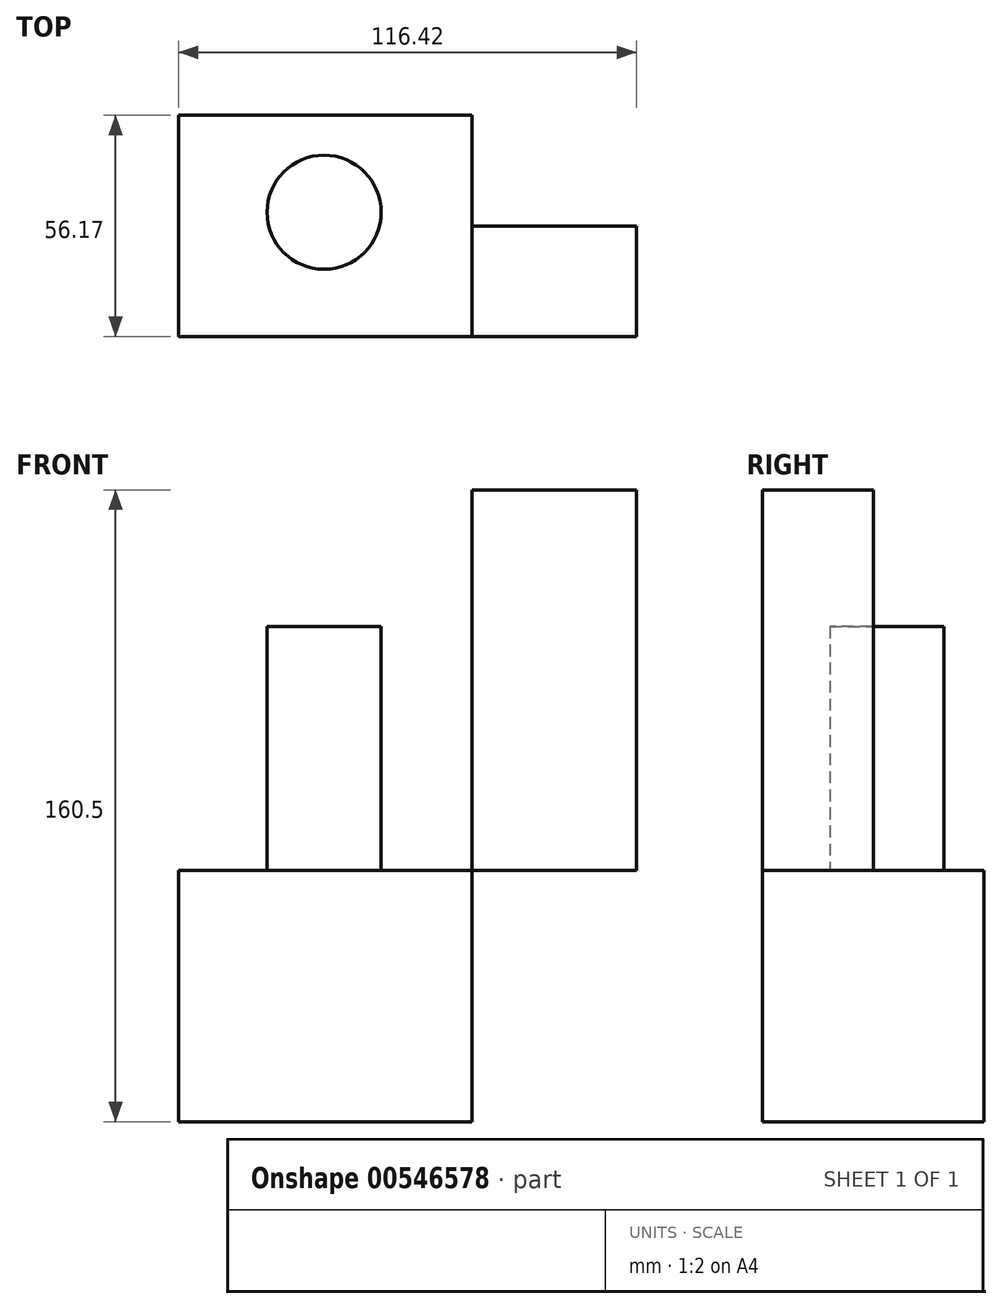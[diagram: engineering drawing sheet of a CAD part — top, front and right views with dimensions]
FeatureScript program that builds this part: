
annotation { "Feature Type Name" : "Feature", "Feature Type Description" : "" }
export const myFeature = defineFeature(function(context is Context, id is Id, definition is map)
    precondition{}
    {
        {
            var Q0;
            Q0=qCreatedBy(makeId("Right.planeOp"),FACE);
            var sketch = newSketch(context, id + "F0", { "sketchPlane" : qUnion([Q0])});
            skLineSegment(sketch, "E0.bottom", {"start": v(56.17, 0) * mm, "end": v(0, 0) * mm});
            skLineSegment(sketch, "E0.top", {"start": v(56.17, 63.78) * mm, "end": v(0, 63.78) * mm});
            skLineSegment(sketch, "E0.left", {"start": v(56.17, 0) * mm, "end": v(56.17, 63.78) * mm});
            skLineSegment(sketch, "E0.right", {"start": v(0, 0) * mm, "end": v(0, 63.78) * mm});
            skSolve(sketch);
        }
        {
            var Q0;
            Q0=makeQuery(id+"F0.imprint","IMPRINT",FACE,{"disambiguationData":[TD([[makeQuery(id+"F0.imprint","IMPRINT",EDGE,{"derivedFrom":sQuery(id+"F0.wireOp",EDGE,"E0.bottom")}),-1.0]])]});
            extrude(context, id + "F1", {"entities" : qUnion([Q0]), "depth" : 74.57 * mm, "offsetDistance" : 25.4 * mm});
        }
        {
            var Q0;
            Q0=makeQuery(id+"F1.opExtrude","SWEPT_FACE",FACE,{"disambiguationData":[OSD([sQuery(id+"F0.wireOp",EDGE,"E0.top")])]});
            var sketch = newSketch(context, id + "F2", { "sketchPlane" : qUnion([Q0])});
            skLineSegment(sketch, "E1.bottom", {"start": v(74.57, 28.09) * mm, "end": v(116.42, 28.09) * mm});
            skLineSegment(sketch, "E1.top", {"start": v(74.57, 0) * mm, "end": v(116.42, 0) * mm});
            skLineSegment(sketch, "E1.left", {"start": v(74.57, 28.09) * mm, "end": v(74.57, 0) * mm});
            skLineSegment(sketch, "E1.right", {"start": v(116.42, 28.09) * mm, "end": v(116.42, 0) * mm});
            skSolve(sketch);
        }
        {
            var Q0;
            Q0 = qSketchRegion(id + "F2", true);
            extrude(context, id + "F3", {"entities" : qUnion([Q0]), "depth" : 96.72 * mm, "offsetDistance" : 25.4 * mm});
        }
        {
            var Q0;
            Q0=makeQuery(id+"F1.opExtrude","SWEPT_FACE",FACE,{"disambiguationData":[OSD([sQuery(id+"F0.wireOp",EDGE,"E0.top")])]});
            var sketch = newSketch(context, id + "F4", { "sketchPlane" : qUnion([Q0])});
            skCircle(sketch, "E2", {"center": v(37, 31.56) * mm, "radius": 14.49 * mm});
            skSolve(sketch);
        }
        {
            var Q0;
            Q0=makeQuery(id+"F4.imprint","IMPRINT",FACE,{"disambiguationData":[TD([[makeQuery(id+"F4.imprint","IMPRINT",EDGE,{"derivedFrom":sQuery(id+"F4.wireOp",EDGE,"E2")}),1.0]])]});
            extrude(context, id + "F5", {"entities" : qUnion([Q0]), "operationType" : NewBodyOperationType.ADD, "depth" : 62.03 * mm, "offsetDistance" : 25.4 * mm});
        }
    });
